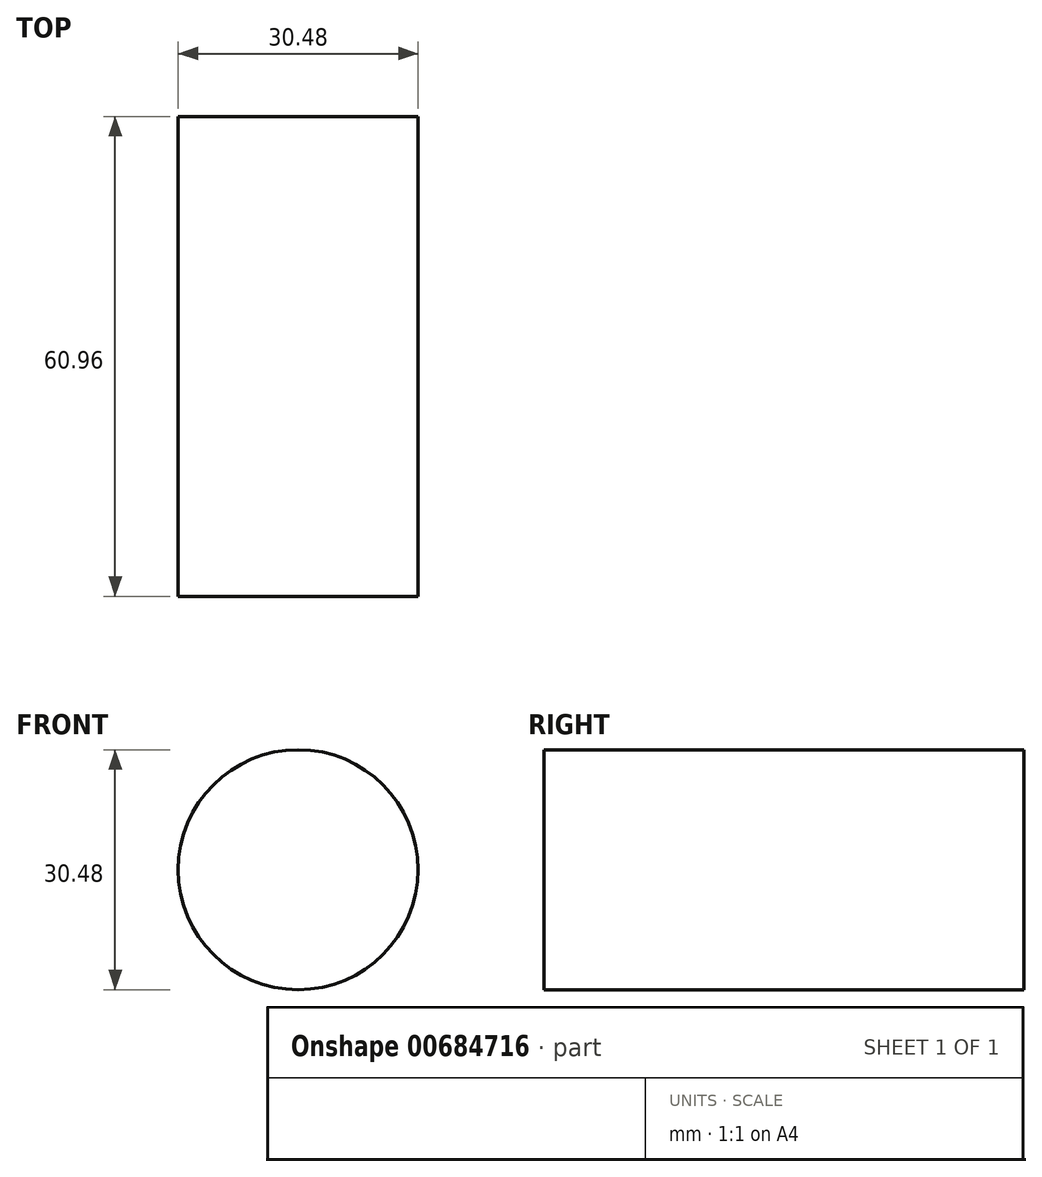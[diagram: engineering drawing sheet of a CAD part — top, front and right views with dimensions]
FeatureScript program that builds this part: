
annotation { "Feature Type Name" : "Feature", "Feature Type Description" : "" }
export const myFeature = defineFeature(function(context is Context, id is Id, definition is map)
    precondition{}
    {
        {
            var Q0;
            Q0=qCreatedBy(makeId("Front.planeOp"),FACE);
            var sketch = newSketch(context, id + "F0", { "sketchPlane" : qUnion([Q0])});
            skCircle(sketch, "E0", {"center": v(0, 0) * mm, "radius": 15.24 * mm});
            skSolve(sketch);
        }
        {
            var Q0;
            Q0 = qSketchRegion(id + "F0", true);
            extrude(context, id + "F1", {"entities" : qUnion([Q0]), "depth" : 60.96 * mm, "offsetDistance" : 30.48 * mm});
        }
    });
